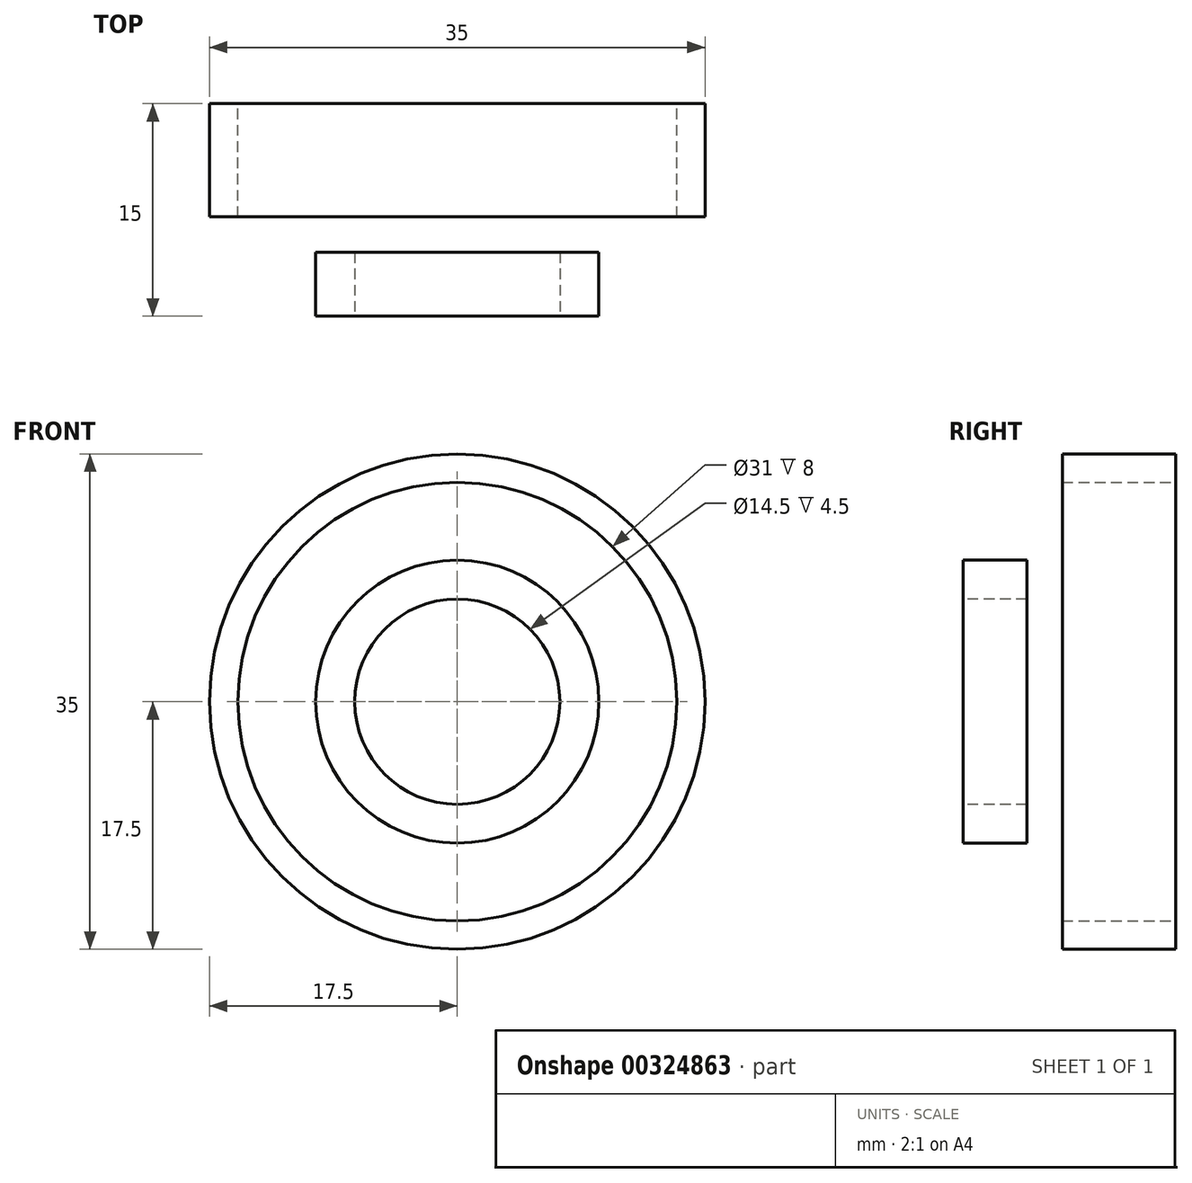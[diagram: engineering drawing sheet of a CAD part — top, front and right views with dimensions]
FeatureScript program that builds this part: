
annotation { "Feature Type Name" : "Feature", "Feature Type Description" : "" }
export const myFeature = defineFeature(function(context is Context, id is Id, definition is map)
    precondition{}
    {
        {
            var Q0;
            Q0=qCreatedBy(makeId("Front.planeOp"),FACE);
            var sketch = newSketch(context, id + "F0", { "sketchPlane" : qUnion([Q0])});
            skCircle(sketch, "E0", {"center": v(0, 0) * mm, "radius": 17.5 * mm});
            skSolve(sketch);
        }
        {
            var Q0;
            Q0=makeQuery(id+"F0.imprint","IMPRINT",FACE,{"disambiguationData":[TD([[makeQuery(id+"F0.imprint","IMPRINT",EDGE,{"derivedFrom":sQuery(id+"F0.wireOp",EDGE,"E0")}),1.0]])]});
            extrude(context, id + "F1", {"entities" : qUnion([Q0]), "depth" : 8 * mm});
        }
        {
            var Q0;
            Q0=makeQuery(id+"F1.opExtrude","CAP_FACE",FACE,{"disambiguationData":[OSD([sQuery(id+"F0.wireOp",EDGE,"E0")])],"isStart":false});
            var sketch = newSketch(context, id + "F2", { "sketchPlane" : qUnion([Q0])});
            skCircle(sketch, "E1", {"center": v(0, 0) * mm, "radius": 10 * mm});
            skSolve(sketch);
        }
        {
            var Q0;
            Q0=makeQuery(id+"F2.imprint","IMPRINT",FACE,{"disambiguationData":[TD([[makeQuery(id+"F2.imprint","IMPRINT",EDGE,{"derivedFrom":sQuery(id+"F2.wireOp",EDGE,"E1")}),1.0]])]});
            extrude(context, id + "F3", {"entities" : qUnion([Q0]), "operationType" : NewBodyOperationType.ADD, "depth" : 7 * mm});
        }
        {
            var Q0;
            Q0=makeQuery(id+"F3.opExtrude","CAP_FACE",FACE,{"disambiguationData":[OSD([sQuery(id+"F2.wireOp",EDGE,"E1")])],"isStart":false});
            var sketch = newSketch(context, id + "F4", { "sketchPlane" : qUnion([Q0])});
            skCircle(sketch, "E2", {"center": v(0, 0) * mm, "radius": 7.25 * mm});
            skSolve(sketch);
        }
        {
            var Q0;
            Q0=makeQuery(id+"F4.imprint","IMPRINT",FACE,{"disambiguationData":[TD([[makeQuery(id+"F4.imprint","IMPRINT",EDGE,{"derivedFrom":sQuery(id+"F4.wireOp",EDGE,"E2")}),1.0]])]});
            extrude(context, id + "F5", {"entities" : qUnion([Q0]), "operationType" : NewBodyOperationType.REMOVE, "oppositeDirection" : true, "depth" : 25 * mm});
        }
        {
            var Q0;
            Q0=makeQuery(id+"F1.opExtrude","CAP_FACE",FACE,{"disambiguationData":[OSD([sQuery(id+"F0.wireOp",EDGE,"E0")])],"isStart":true});
            var sketch = newSketch(context, id + "F6", { "sketchPlane" : qUnion([Q0])});
            skCircle(sketch, "E3", {"center": v(0, 0) * mm, "radius": 15.5 * mm});
            skSolve(sketch);
        }
        {
            var Q0;
            Q0=makeQuery(id+"F6.imprint","IMPRINT",FACE,{"disambiguationData":[TD([[makeQuery(id+"F6.imprint","IMPRINT",EDGE,{"derivedFrom":sQuery(id+"F6.wireOp",EDGE,"E3")}),1.0]])]});
            extrude(context, id + "F7", {"entities" : qUnion([Q0]), "operationType" : NewBodyOperationType.REMOVE, "oppositeDirection" : true, "depth" : 10.5 * mm});
        }
    });
